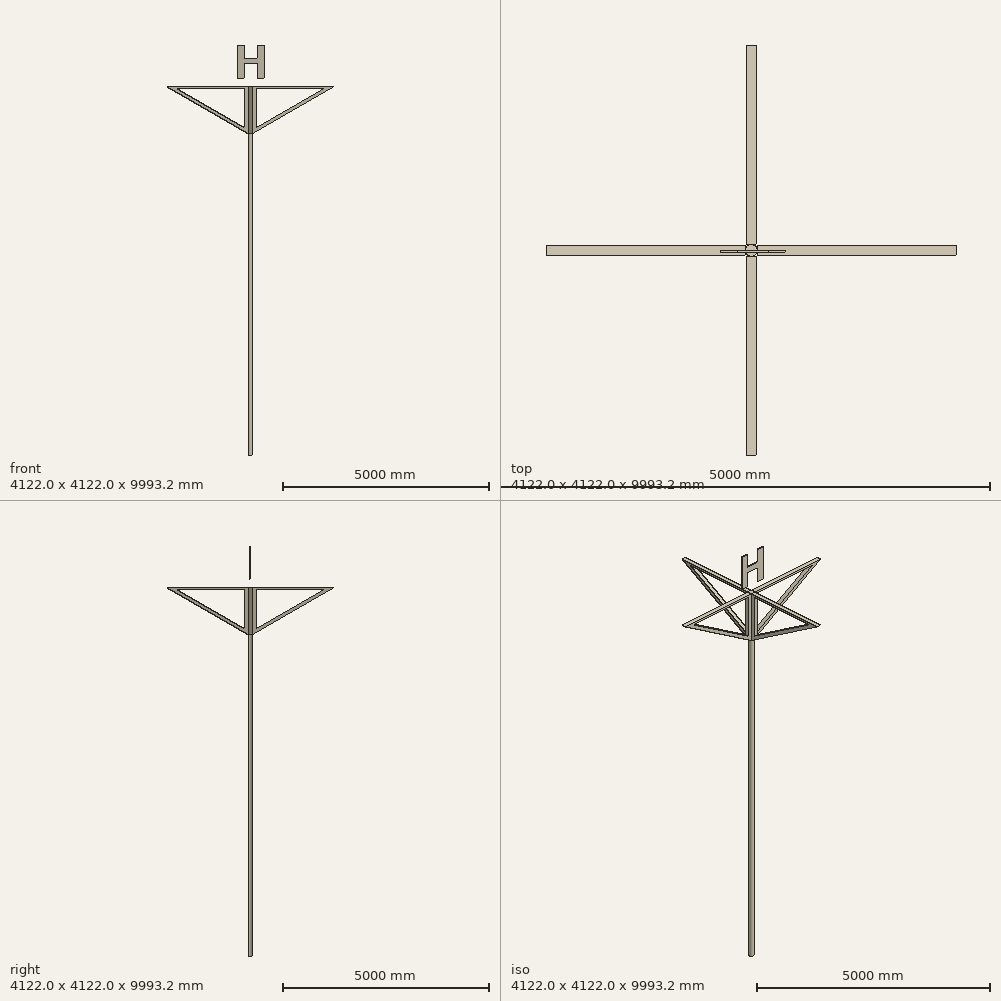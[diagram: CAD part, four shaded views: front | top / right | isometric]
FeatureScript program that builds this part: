
annotation { "Feature Type Name" : "Feature", "Feature Type Description" : "" }
export const myFeature = defineFeature(function(context is Context, id is Id, definition is map)
    precondition{}
    {
        {
            var Q0;
            Q0=qCreatedBy(makeId("Top.planeOp"),FACE);
            var sketch = newSketch(context, id + "F0", { "sketchPlane" : qUnion([Q0])});
            skCircle(sketch, "E0", {"center": v(0, 0) * mm, "radius": 60.5 * mm});
            skSolve(sketch);
        }
        {
            var Q0;
            Q0 = qSketchRegion(id + "F0", true);
            extrude(context, id + "F1", {"entities" : qUnion([Q0]), "depth" : 9000 * mm, "offsetDistance" : 25 * mm});
        }
        {
            var Q0;
            Q0=qCreatedBy(makeId("Front.planeOp"),FACE);
            var sketch = newSketch(context, id + "F2", { "sketchPlane" : qUnion([Q0])});
            skLineSegment(sketch, "E1", {"start": v(60.5, 9000) * mm, "end": v(60.5, 7845) * mm});
            skLineSegment(sketch, "E2", {"start": v(60.5, 7845) * mm, "end": v(2061.02, 9000) * mm});
            skLineSegment(sketch, "E3", {"start": v(2061.02, 9000) * mm, "end": v(60.5, 9000) * mm});
            skLineSegment(sketch, "E4", {"start": v(60.5, 9000) * mm, "end": v(60.5, 0) * mm, "construction": true});
            skLineSegment(sketch, "E5", {"start": v(-60.5, 0) * mm, "end": v(-60.5, 9000) * mm});
            skLineSegment(sketch, "E6", {"start": v(140.5, 8950) * mm, "end": v(140.5, 7983.56) * mm});
            skLineSegment(sketch, "E7", {"start": v(140.5, 7983.56) * mm, "end": v(1814.42, 8950) * mm});
            skLineSegment(sketch, "E8", {"start": v(1814.42, 8950) * mm, "end": v(140.5, 8950) * mm});
            skSolve(sketch);
        }
        {
            var Q0;
            Q0 = qSketchRegion(id + "F2", true);
            extrude(context, id + "F3", {"entities" : qUnion([Q0]), "operationType" : NewBodyOperationType.ADD, "endBound" : BoundingType.SYMMETRIC, "depth" : 100 * mm, "offsetDistance" : 25 * mm});
        }
        {
            var Q0;
            Q0=makeQuery(id+"F3.opExtrude","SWEPT_BODY",BODY,{"disambiguationData":[OSD([sQuery(id+"F2.wireOp",EDGE,"E1"),sQuery(id+"F2.wireOp",EDGE,"E2"),sQuery(id+"F2.wireOp",EDGE,"E3"),sQuery(id+"F2.wireOp",EDGE,"E6"),sQuery(id+"F2.wireOp",EDGE,"E7"),sQuery(id+"F2.wireOp",EDGE,"E8")])]});
            var Q1;
            Q1=makeQuery(id+"F1.opExtrude","SWEPT_FACE",FACE,{"disambiguationData":[OSD([sQuery(id+"F0.wireOp",EDGE,"E0")])]});
            circularPattern(context, id + "F4", {"entities" : qUnion([Q0]), "axis" : qUnion([Q1]), "angle" : 360 * degree, "instanceCount" : 4, "equalSpace" : true});
        }
        {
            var Q0;
            Q0=qCreatedBy(makeId("Front.planeOp"),FACE);
            var sketch = newSketch(context, id + "F5", { "sketchPlane" : qUnion([Q0])});
            skText(sketch, "E9", { "text": "H", "fontName": "OpenSans-Bold.ttf"});
            const initialGuessF5  = {"E9": [-0.41094, 9.2, 1, 0, 0.8]};
            skSetInitialGuess(sketch, initialGuessF5);
            skSolve(sketch);
        }
        {
            var Q0;
            Q0 = qSketchRegion(id + "F5", true);
            extrude(context, id + "F6", {"entities" : qUnion([Q0]), "depth" : 25 * mm, "offsetDistance" : 25 * mm});
        }
    });
